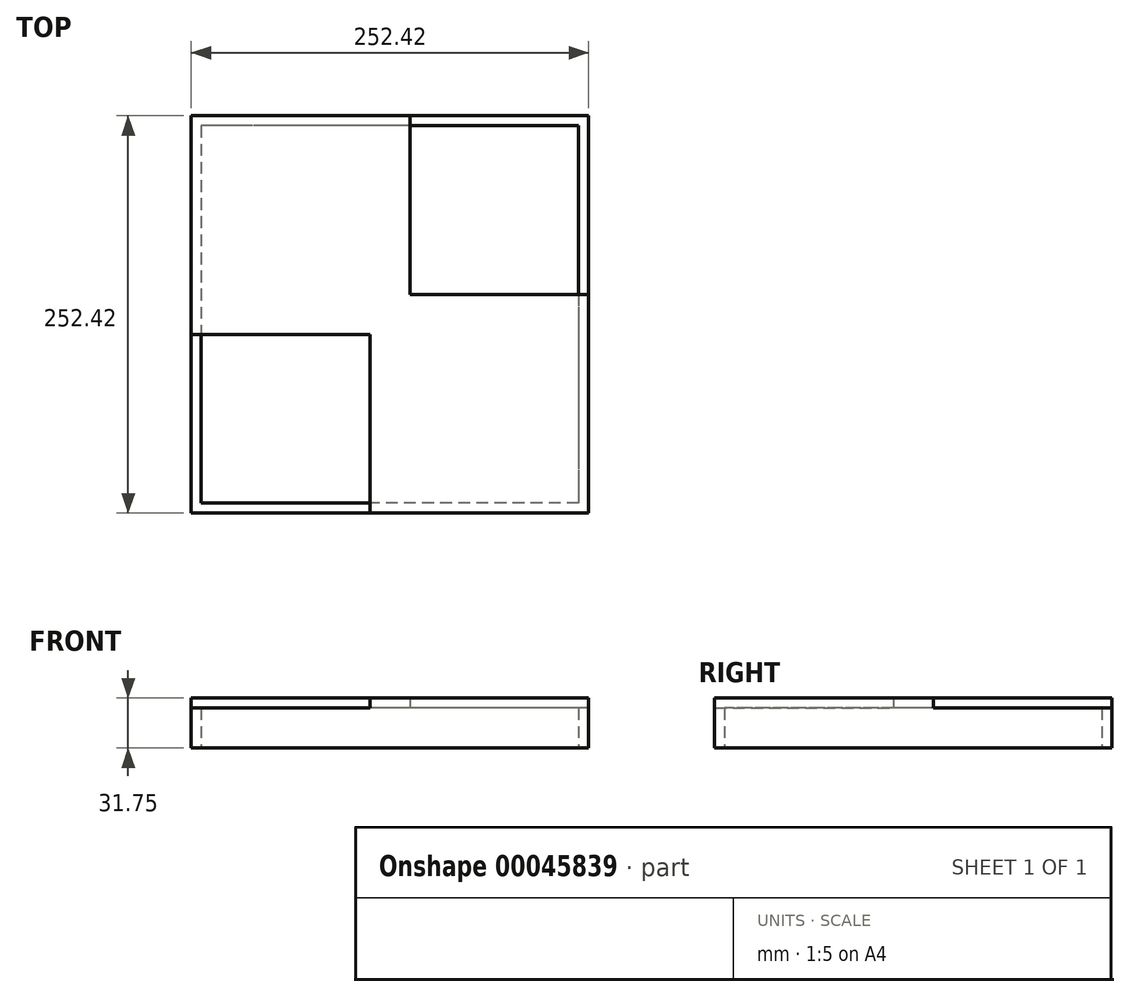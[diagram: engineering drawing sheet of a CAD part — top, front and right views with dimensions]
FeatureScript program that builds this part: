
annotation { "Feature Type Name" : "Feature", "Feature Type Description" : "" }
export const myFeature = defineFeature(function(context is Context, id is Id, definition is map)
    precondition{}
    {
        {
            var Q0;
            Q0=qCreatedBy(makeId("Top.planeOp"),FACE);
            var sketch = newSketch(context, id + "F0", { "sketchPlane" : qUnion([Q0])});
            skLineSegment(sketch, "E0.rect.bottom", {"start": v(126.2, -126.2) * mm, "end": v(-126.2, -126.2) * mm});
            skLineSegment(sketch, "E0.rect.top", {"start": v(126.2, 126.2) * mm, "end": v(-126.2, 126.2) * mm});
            skLineSegment(sketch, "E0.rect.left", {"start": v(126.2, -126.2) * mm, "end": v(126.2, 126.2) * mm});
            skLineSegment(sketch, "E0.rect.right", {"start": v(-126.2, -126.2) * mm, "end": v(-126.2, 126.2) * mm});
            skPoint(sketch, "E0.rect.middle", {"position": v(0, 0) * mm});
            skLineSegment(sketch, "E1.rect.bottom", {"start": v(119.86, 119.86) * mm, "end": v(-119.86, 119.86) * mm});
            skLineSegment(sketch, "E1.rect.top", {"start": v(119.86, -119.86) * mm, "end": v(-119.86, -119.86) * mm});
            skLineSegment(sketch, "E1.rect.left", {"start": v(119.86, 119.86) * mm, "end": v(119.86, -119.86) * mm});
            skLineSegment(sketch, "E1.rect.right", {"start": v(-119.86, 119.86) * mm, "end": v(-119.86, -119.86) * mm});
            skLineSegment(sketch, "E2", {"start": v(119.86, 119.86) * mm, "end": v(119.86, 126.2) * mm, "construction": true});
            skLineSegment(sketch, "E3", {"start": v(119.86, 119.86) * mm, "end": v(126.2, 119.86) * mm, "construction": true});
            skSolve(sketch);
        }
        {
            var Q0;
            Q0=qSketchRegion(id+"F0",true);
            extrude(context, id + "F1", {"entities" : qUnion([Q0]), "depth" : 25.4 * mm});
        }
        {
            var Q0;
            Q0=makeQuery(id+"F1.opExtrude","CAP_FACE",FACE,{"disambiguationData":[OSD([sQuery(id+"F0.wireOp",EDGE,"E0.rect.bottom"),sQuery(id+"F0.wireOp",EDGE,"E0.rect.top"),sQuery(id+"F0.wireOp",EDGE,"E0.rect.left"),sQuery(id+"F0.wireOp",EDGE,"E0.rect.right"),sQuery(id+"F0.wireOp",EDGE,"E1.rect.bottom"),sQuery(id+"F0.wireOp",EDGE,"E1.rect.top"),sQuery(id+"F0.wireOp",EDGE,"E1.rect.left"),sQuery(id+"F0.wireOp",EDGE,"E1.rect.right")])],"isStart":false});
            var sketch = newSketch(context, id + "F2", { "sketchPlane" : qUnion([Q0])});
            skLineSegment(sketch, "E4.bottom", {"start": v(-126.2, 126.2) * mm, "end": v(12.7, 126.2) * mm});
            skLineSegment(sketch, "E4.top", {"start": v(-126.2, -12.7) * mm, "end": v(-12.7, -12.7) * mm});
            skLineSegment(sketch, "E4.left", {"start": v(-126.2, 126.2) * mm, "end": v(-126.2, -12.7) * mm});
            skLineSegment(sketch, "E4.right", {"start": v(12.7, 126.2) * mm, "end": v(12.7, 12.7) * mm});
            skLineSegment(sketch, "E5.bottom", {"start": v(126.2, -126.2) * mm, "end": v(-12.7, -126.2) * mm});
            skLineSegment(sketch, "E5.top", {"start": v(126.2, 12.7) * mm, "end": v(12.7, 12.7) * mm});
            skLineSegment(sketch, "E5.left", {"start": v(126.2, -126.2) * mm, "end": v(126.2, 12.7) * mm});
            skLineSegment(sketch, "E5.right", {"start": v(-12.7, -126.2) * mm, "end": v(-12.7, -12.7) * mm});
            skLineSegment(sketch, "E6.bottom", {"start": v(-12.7, -12.7) * mm, "end": v(12.7, -12.7) * mm, "construction": true});
            skLineSegment(sketch, "E6.top", {"start": v(-12.7, 12.7) * mm, "end": v(12.7, 12.7) * mm, "construction": true});
            skLineSegment(sketch, "E6.left", {"start": v(-12.7, -12.7) * mm, "end": v(-12.7, 12.7) * mm, "construction": true});
            skLineSegment(sketch, "E6.right", {"start": v(12.7, -12.7) * mm, "end": v(12.7, 12.7) * mm, "construction": true});
            skSolve(sketch);
        }
        {
            var Q0;
            Q0=qSketchRegion(id+"F2",true);
            extrude(context, id + "F3", {"entities" : qUnion([Q0]), "operationType" : NewBodyOperationType.ADD, "depth" : 6.35 * mm});
        }
    });
